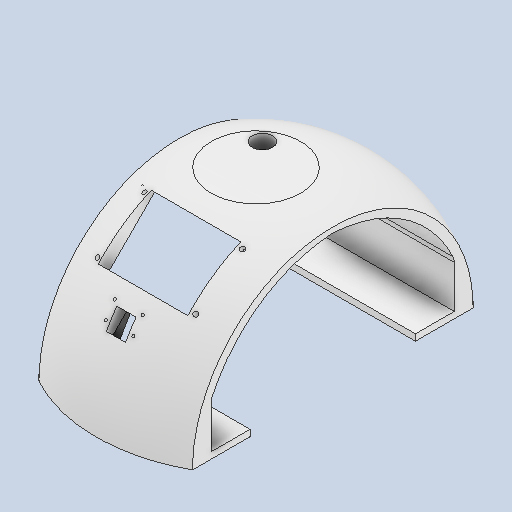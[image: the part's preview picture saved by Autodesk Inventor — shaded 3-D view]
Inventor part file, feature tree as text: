
AUTODESK INVENTOR PART (.ipt)
format: ipt  version: 2023 (Build 270158000, 158)  size: 530,432 bytes
history: native  units: mm
features: sketch x17, extrude x12, hole x4, fillet x3, other x1, revolve x1
ambient origin geometry x8: Origin, YZ Plane, XZ Plane, XY Plane, X Axis, Y Axis, Z Axis, Center Point
bodies: Body1 (feature_tree)
feature tree (38):
  other  "ソリッド1"
  revolve  "回転1"
  extrude  "押し出し1"  Depth=125.0mm
  extrude  "押し出し2"  TaperAngle=180.0deg  [1 undecoded]
  extrude  "押し出し3"  TaperAngle=45.0deg  [1 undecoded]
  extrude  "押し出し4"  Depth=125.0mm
  extrude  "押し出し5"  Depth=120.0mm
  hole  "穴1"  [1 undecoded]
  extrude  "押し出し6"  TaperAngle=90.0deg  [1 undecoded]
  extrude  "押し出し7"  Depth=120.0mm
  fillet  "フィレット1"  Radius=250.0mm
  fillet  "フィレット2"  Radius=200.0mm
  extrude  "押し出し8"  TaperAngle=135.0deg  [1 undecoded]
  hole  "穴2"  [1 undecoded]
  extrude  "押し出し9"  Depth=70.0mm
  extrude  "押し出し10"  Depth=50.0mm
  extrude  "押し出し11"  Depth=60.0mm
  fillet  "フィレット3"  Radius=20.0mm
  hole  "穴3"  [1 undecoded]
  hole  "穴4"  [1 undecoded]
  extrude  "押し出し13"  Depth=15.0mm
  sketch  "スケッチ1"
  sketch  "スケッチ2"
  sketch  "スケッチ3"
  sketch  "スケッチ4"
  sketch  "スケッチ5"
  sketch  "スケッチ6"
  sketch  "スケッチ7"
  sketch  "スケッチ8"
  sketch  "スケッチ9"
  sketch  "スケッチ11"
  sketch  "スケッチ12"
  sketch  "スケッチ13"
  sketch  "スケッチ14"
  sketch  "スケッチ15"
  sketch  "スケッチ17"
  sketch  "スケッチ18"
  sketch  "スケッチ19"
note: 8 required parameter values undecoded (feature->parameter linkage not recoverable at this tier; creation-order binding heuristic only, values carry confidence <= 0.55)
